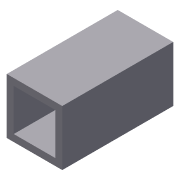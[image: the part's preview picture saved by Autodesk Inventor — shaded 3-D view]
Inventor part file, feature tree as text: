
AUTODESK INVENTOR PART (.ipt)
format: ipt  version: 2012 (Build 160160000, 160)  size: 71,680 bytes
history: native  units: in
note: dims shown in document units (in); Inventor stores cm internally (conversion verified against a paired STEP export)
features: extrude x1, shell x1, sketch x1
ambient origin geometry x8: Origin, YZ Plane, XZ Plane, XY Plane, X Axis, Y Axis, Z Axis, Center Point
bodies: Solid1 (feature_tree)
feature tree (3):
  extrude  "Extrusion1"  Depth=1.0in
  shell  "Shell1"  Thickness=2.0in
  sketch  "Sketch1"  dims[d0=1.0in d1=1.0in d2=2.0in d3=0.0in d4=0.125in]
